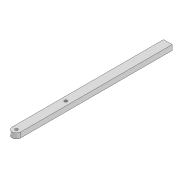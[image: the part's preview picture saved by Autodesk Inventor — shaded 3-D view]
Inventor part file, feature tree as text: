
AUTODESK INVENTOR PART (.ipt)
format: ipt  version: 2022 (Build 260153000, 153)  size: 99,840 bytes
history: native  units: mm
features: extrude x2, sketch x2
ambient origin geometry x8: Origin, YZ Plane, XZ Plane, XY Plane, X Axis, Y Axis, Z Axis, Center Point
bodies: Solid1 (feature_tree)
feature tree (4):
  extrude  "Extrusion1"  Depth=3.3mm
  extrude  "Extrusion2"  Depth=355.998mm
  sketch  "Sketch1"  dims[d0=3.3mm d1=3.3mm]
  sketch  "Sketch2"  dims[d2=10.0mm d3=355.998mm d6=6.0mm d7=0.0mm d14=3.3mm d15=57.376mm d16=10.0mm d17=0.0mm]
